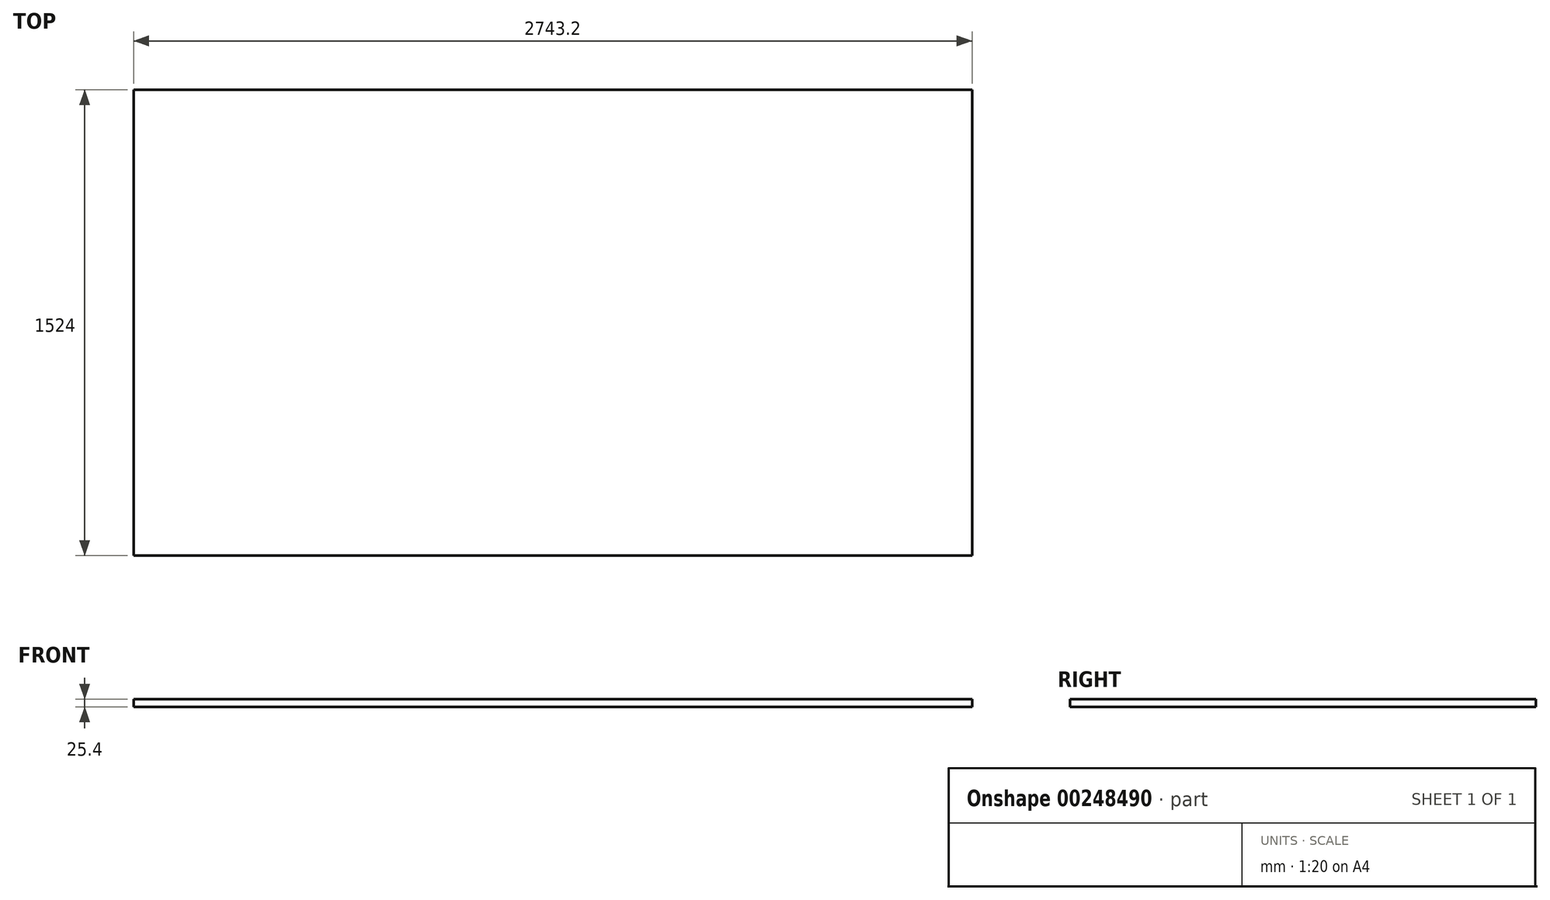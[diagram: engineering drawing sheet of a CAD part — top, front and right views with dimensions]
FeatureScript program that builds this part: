
annotation { "Feature Type Name" : "Feature", "Feature Type Description" : "" }
export const myFeature = defineFeature(function(context is Context, id is Id, definition is map)
    precondition{}
    {
        {
            var Q0;
            Q0=qCreatedBy(makeId("Top.planeOp"),FACE);
            var sketch = newSketch(context, id + "F0", { "sketchPlane" : qUnion([Q0])});
            skLineSegment(sketch, "E0.bottom", {"start": v(-144.11, 1429.68) * mm, "end": v(2599.09, 1429.68) * mm});
            skLineSegment(sketch, "E0.top", {"start": v(-144.11, -94.32) * mm, "end": v(2599.09, -94.32) * mm});
            skLineSegment(sketch, "E0.left", {"start": v(-144.11, 1429.68) * mm, "end": v(-144.11, -94.32) * mm});
            skLineSegment(sketch, "E0.right", {"start": v(2599.09, 1429.68) * mm, "end": v(2599.09, -94.32) * mm});
            skSolve(sketch);
        }
        {
            var Q0;
            Q0 = qSketchRegion(id + "F0", true);
            extrude(context, id + "F1", {"entities" : qUnion([Q0]), "depth" : 25.4 * mm});
        }
    });
